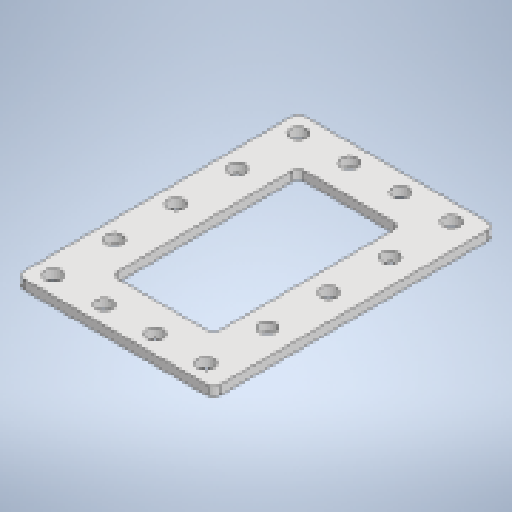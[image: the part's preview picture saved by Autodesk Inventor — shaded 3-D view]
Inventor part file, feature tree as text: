
AUTODESK INVENTOR PART (.ipt)
format: ipt  version: 2025.4 (Build 294407000, 407)  size: 251,904 bytes
history: native  units: mm
features: sketch x3, other x3, sheet_metal_op x1, chamfer x1, projected_geometry x1
ambient origin geometry x8: Origin, YZ Plane, XZ Plane, XY Plane, X Axis, Y Axis, Z Axis, Center Point
bodies: Body1 (feature_tree)
feature tree (9):
  sheet_metal_op  "Face2"
  chamfer  "Corner Round1"
  sketch  "Sketch2"  dims[d29=108.0mm]
  other  "Plate2"
  sketch  "Sketch5"  dims[d30=202.0mm d31=50.0mm d33=17.0mm d34=19.0mm d35=66.0mm d36=66.0mm d37=40.0mm d39=54.0mm d40=10.0mm d42=10.0mm d44=10.0mm d45=0.0mm d46=6.0mm d47=208.0mm d48=302.0mm]
  projected_geometry  "Projected Loop1"
  sketch  "Sketch Rectangular Pattern1"  dims[d14=10.0mm]
  other  "Cut3"
  other  "Definition1"
